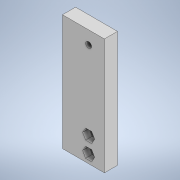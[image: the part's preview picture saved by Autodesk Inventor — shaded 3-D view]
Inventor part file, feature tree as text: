
AUTODESK INVENTOR PART (.ipt)
format: ipt  version: 2020 (Build 240168000, 168)  size: 137,216 bytes
history: native  units: mm
features: other x4, mirror x1
ambient origin geometry x8: Origin, YZ Plane, XZ Plane, XY Plane, X Axis, Y Axis, Z Axis, Center Point
bodies: Body1 (feature_tree)
feature tree (5):
  other  "jenga_R.ipt"
  mirror  "미러1"
  other  "솔리드1::jenga_R.ipt"
  other  "피쳐 태그1"
  other  "솔리드1"
